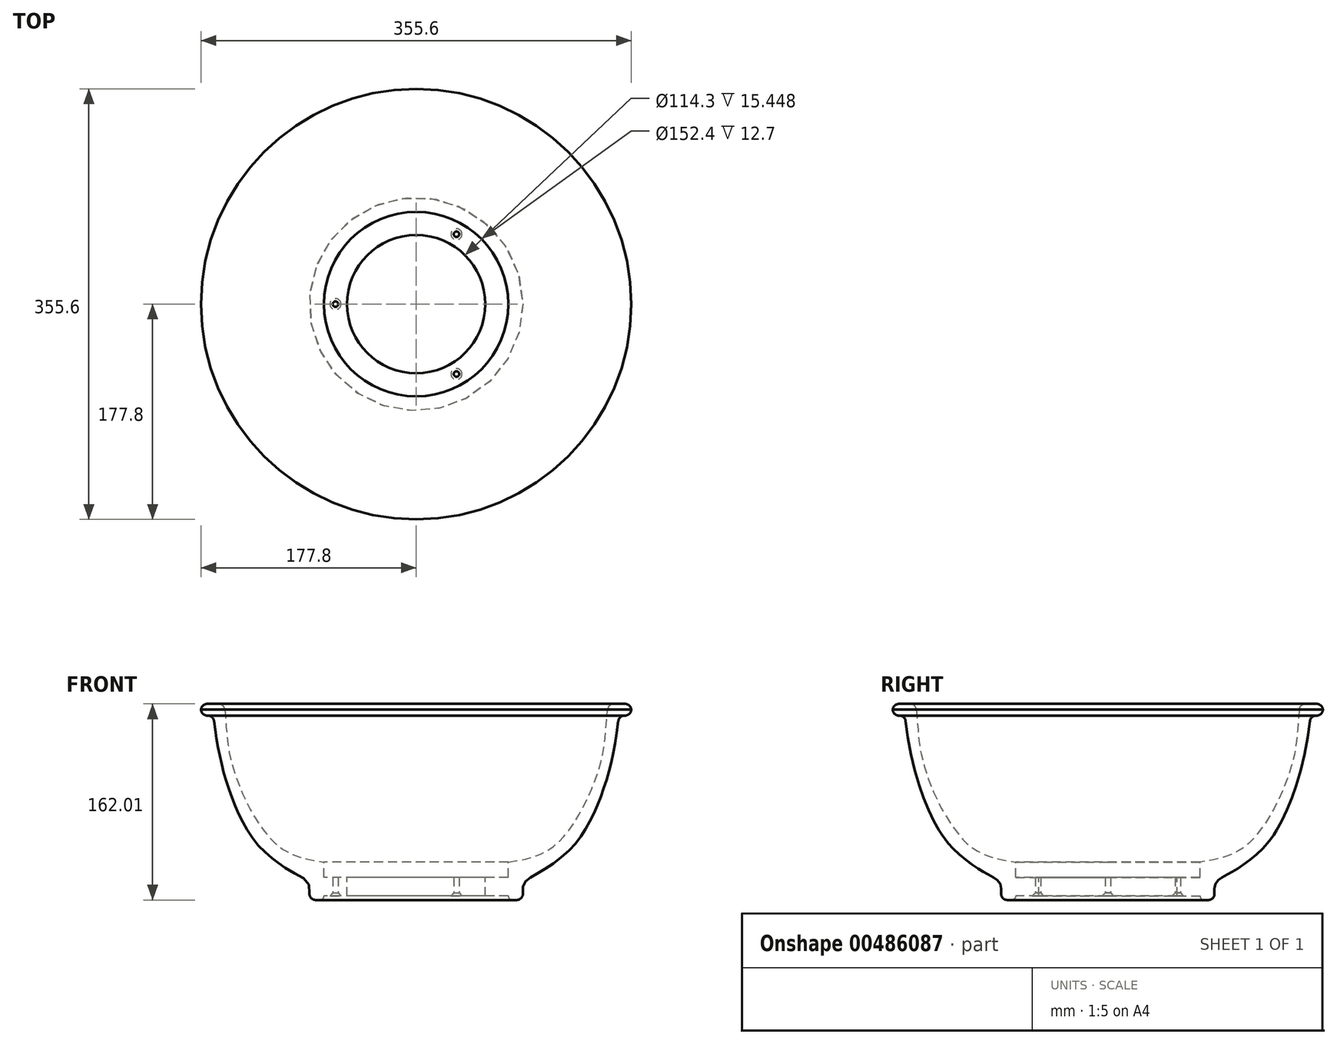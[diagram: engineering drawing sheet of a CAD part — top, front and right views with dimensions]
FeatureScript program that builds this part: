
annotation { "Feature Type Name" : "Feature", "Feature Type Description" : "" }
export const myFeature = defineFeature(function(context is Context, id is Id, definition is map)
    precondition{}
    {
        {
            var Q0;
            Q0=qCreatedBy(makeId("Front.planeOp"),FACE);
            var sketch = newSketch(context, id + "F0", { "sketchPlane" : qUnion([Q0])});
            skLineSegment(sketch, "E0", {"start": v(46.68, -56.98) * mm, "end": v(46.68, -37.93) * mm});
            skLineSegment(sketch, "E1", {"start": v(46.68, -37.93) * mm, "end": v(27.63, -37.93) * mm});
            skLineSegment(sketch, "E2", {"start": v(27.63, -37.93) * mm, "end": v(27.63, -25.23) * mm});
            skFitSpline(sketch, "E3", {"points": [v(27.63, -25.23) * mm, v(-1.8, -17.35) * mm, v(-19.94, -2.15) * mm, v(-39.3, 30.45) * mm, v(-51.07, 67.22) * mm, v(-54.92, 105.38) * mm], "startDerivative": vector(-189.68, 21.22) * mm, "endDerivative": vector(-27.24, 248.45) * mm});
            skLineSegment(sketch, "E4", {"start": v(-54.92, 105.38) * mm, "end": v(-73.97, 105.38) * mm});
            skLineSegment(sketch, "E5", {"start": v(-73.97, 105.38) * mm, "end": v(-73.97, 95.72) * mm});
            skLineSegment(sketch, "E6", {"start": v(-73.97, 95.72) * mm, "end": v(-63.81, 95.72) * mm});
            skFitSpline(sketch, "E7", {"points": [v(14.93, -56.63) * mm, v(14.93, -43.55) * mm, v(3.08, -34.5) * mm, v(-23.32, -14.94) * mm, v(-39.01, 6.9) * mm, v(-49.8, 31.43) * mm, v(-57.39, 57.18) * mm, v(-63.81, 95.72) * mm], "startDerivative": vector(14.9, 94.42) * mm, "endDerivative": vector(-30.73, 264.01) * mm});
            skLineSegment(sketch, "E8", {"start": v(14.93, -56.63) * mm, "end": v(27.63, -56.63) * mm});
            skLineSegment(sketch, "E9", {"start": v(27.63, -56.63) * mm, "end": v(27.63, -53.37) * mm});
            skLineSegment(sketch, "E10", {"start": v(27.63, -53.37) * mm, "end": v(46.68, -53.37) * mm});
            skLineSegment(sketch, "E11", {"start": v(103.83, -59.02) * mm, "end": v(103.83, -56.98) * mm, "construction": true});
            skLineSegment(sketch, "E12", {"start": v(103.83, 108.12) * mm, "end": v(103.83, -56.98) * mm, "construction": true});
            skPoint(sketch, "E13", {"position": v(103.83, -25.23) * mm});
            skSolve(sketch);
        }
        {
            var Q0;
            {var subQ0=sQuery(id+"F0.wireOp",EDGE,"E1");Q0=makeQuery(id+"F0.imprint","IMPRINT",FACE,{"disambiguationData":[TD([[makeQuery(id+"F0.imprint","IMPRINT",EDGE,{"derivedFrom":subQ0}),1.0]])]});}
            var Q1;
            Q1=sQuery(id+"F0.wireOp",EDGE,"E12");
            revolve(context, id + "F1", {"entities" : qUnion([Q0]), "axis" : qUnion([Q1]), "revolveType" : RevolveType.FULL});
        }
        {
            var Q0;
            Q0=makeQuery(id+"F1.opRevolve","SWEPT_EDGE",EDGE,{"disambiguationData":[OSD([sQuery(id+"F0.wireOp",EDGE,"E5"),sQuery(id+"F0.wireOp",EDGE,"E6")])]});
            var Q1;
            Q1=makeQuery(id+"F1.opRevolve","SWEPT_EDGE",EDGE,{"disambiguationData":[OSD([sQuery(id+"F0.wireOp",EDGE,"E3"),sQuery(id+"F0.wireOp",EDGE,"E4")])]});
            var Q2;
            Q2=makeQuery(id+"F1.opRevolve","SWEPT_EDGE",EDGE,{"disambiguationData":[OSD([sQuery(id+"F0.wireOp",EDGE,"E7"),sQuery(id+"F0.wireOp",EDGE,"E8")])]});
            var Q3;
            Q3=makeQuery(id+"F1.opRevolve","SWEPT_EDGE",EDGE,{"disambiguationData":[OSD([sQuery(id+"F0.wireOp",EDGE,"E6"),sQuery(id+"F0.wireOp",EDGE,"E7")])]});
            fillet(context, id + "F2", {"entities" : qUnion([Q0, Q1, Q2, Q3]), "radius" : 5.08 * mm, "tangentPropagation" : true, "allowEdgeOverflow" : false});
        }
        {
            var Q0;
            Q0=makeQuery(id+"F1.opRevolve","SWEPT_EDGE",EDGE,{"disambiguationData":[OSD([sQuery(id+"F0.wireOp",EDGE,"E4"),sQuery(id+"F0.wireOp",EDGE,"E5")])]});
            fillet(context, id + "F3", {"entities" : qUnion([Q0]), "radius" : 5.08 * mm, "tangentPropagation" : true, "allowEdgeOverflow" : false});
        }
        {
            var Q0;
            Q0=makeQuery(id+"F1.opRevolve","SWEPT_FACE",FACE,{"disambiguationData":[OSD([sQuery(id+"F0.wireOp",EDGE,"E10")])]});
            var sketch = newSketch(context, id + "F4", { "sketchPlane" : qUnion([Q0])});
            skCircle(sketch, "E14", {"center": v(103.83, 0) * mm, "radius": 66.68 * mm, "construction": true});
            skPoint(sketch, "E15", {"position": v(37.15, 0) * mm});
            skPoint(sketch, "E16.1.0", {"position": v(137.17, -57.74) * mm});
            skPoint(sketch, "E16.2.0", {"position": v(137.17, 57.74) * mm});
            skSolve(sketch);
        }
        {
            var Q0;
            Q0=sQuery(id+"F4.wireOp",VERTEX,"E14.center");
            var Q1;
            Q1=sQuery(id+"F4.wireOp",VERTEX,"E16.2.0");
            var Q2;
            Q2=sQuery(id+"F4.wireOp",VERTEX,"E16.1.0");
            var Q3;
            Q3=sQuery(id+"F4.wireOp",VERTEX,"E15");
            var Q4;
            Q4=makeQuery(id+"F1.opRevolve","SWEPT_BODY",BODY,{"disambiguationData":[OSD([sQuery(id+"F0.wireOp",EDGE,"E0"),sQuery(id+"F0.wireOp",EDGE,"E1"),sQuery(id+"F0.wireOp",EDGE,"E2"),sQuery(id+"F0.wireOp",EDGE,"E3"),sQuery(id+"F0.wireOp",EDGE,"E4"),sQuery(id+"F0.wireOp",EDGE,"E5"),sQuery(id+"F0.wireOp",EDGE,"E6"),sQuery(id+"F0.wireOp",EDGE,"E7"),sQuery(id+"F0.wireOp",EDGE,"E8"),sQuery(id+"F0.wireOp",EDGE,"E9"),sQuery(id+"F0.wireOp",EDGE,"E10")])]});
            hole(context, id + "F5", {"style" : HoleStyle.C_SINK, "endStyle" : HoleEndStyle.THROUGH, "standardTappedOrClearance" : lookupTablePath({ "standard" : "ANSI", "fit" : "Normal (ASME)", "size" : "#8", "type" : "Clearance" }), "standardBlindInLast" : lookupTablePath({ "fit" : "Free", "standard" : "ANSI", "size" : "#8", "type" : "Clearance" }), "holeDiameter" : 4.5 * mm, "cSinkDiameter" : 9.12 * mm, "cSinkAngle" : 82 * degree, "isTappedThrough" : true, "tappedDepth" : 12.7 * mm, "tapClearance" : 3, "locations" : qUnion([Q0, Q1, Q2, Q3]), "scope" : qUnion([Q4])});
        }
        {
            var Q0;
            Q0=makeQuery(id+"F1.opRevolve","SWEPT_EDGE",EDGE,{"disambiguationData":[OSD([sQuery(id+"F0.wireOp",EDGE,"E8"),sQuery(id+"F0.wireOp",EDGE,"E9")])]});
            fillet(context, id + "F6", {"entities" : qUnion([Q0]), "radius" : 3.25 * mm, "tangentPropagation" : true, "allowEdgeOverflow" : false});
        }
    });
